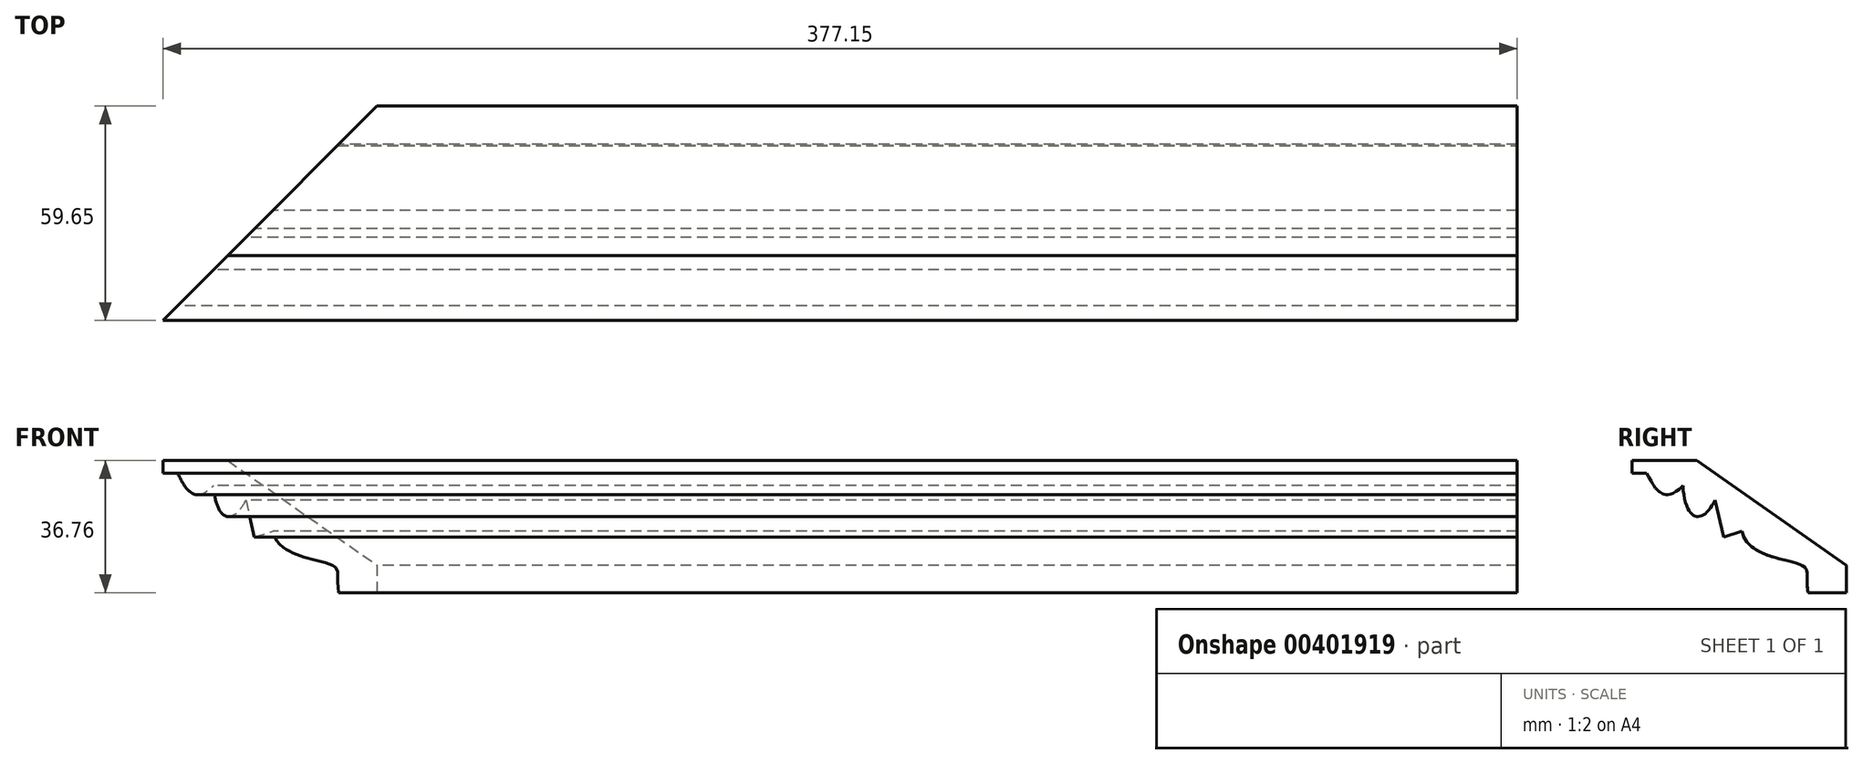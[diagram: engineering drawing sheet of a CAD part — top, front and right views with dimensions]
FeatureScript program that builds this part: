
annotation { "Feature Type Name" : "Feature", "Feature Type Description" : "" }
export const myFeature = defineFeature(function(context is Context, id is Id, definition is map)
    precondition{}
    {
        {
            var Q0;
            Q0=qCreatedBy(makeId("Right.planeOp"),FACE);
            var sketch = newSketch(context, id + "F0", { "sketchPlane" : qUnion([Q0])});
            skLineSegment(sketch, "E0", {"start": v(0, 7.62) * mm, "end": v(-41.61, 36.76) * mm});
            skLineSegment(sketch, "E1", {"start": v(-41.61, 36.76) * mm, "end": v(-59.65, 36.76) * mm});
            skLineSegment(sketch, "E2", {"start": v(-59.65, 36.76) * mm, "end": v(-59.65, 33.27) * mm});
            skLineSegment(sketch, "E3", {"start": v(-59.65, 33.27) * mm, "end": v(-55.58, 33.27) * mm});
            skLineSegment(sketch, "E4", {"start": v(0, 7.62) * mm, "end": v(0, 0) * mm});
            skLineSegment(sketch, "E5", {"start": v(0, 0) * mm, "end": v(-10.67, 0) * mm});
            skFitSpline(sketch, "E6", {"points": [v(-10.67, 0) * mm, v(-11.01, 5.96) * mm, v(-13.27, 7.99) * mm, v(-29.01, 17.09) * mm], "startDerivative": vector(-5.08, 29.03) * mm, "endDerivative": vector(-6.54, 39.72) * mm});
            skLineSegment(sketch, "E7", {"start": v(-29.01, 17.09) * mm, "end": v(-34.16, 15.48) * mm});
            skLineSegment(sketch, "E8", {"start": v(-34.16, 15.48) * mm, "end": v(-36.54, 25.8) * mm});
            skFitSpline(sketch, "E9", {"points": [v(-45.51, 29.77) * mm, v(-52.42, 28.4) * mm, v(-55.58, 33.27) * mm], "startDerivative": vector(-24.15, -24.15) * mm, "endDerivative": vector(-16.65, 31.11) * mm});
            skFitSpline(sketch, "E10", {"points": [v(-45.51, 29.77) * mm, v(-36.54, 25.8) * mm], "startDerivative": vector(2.07, -32.09) * mm, "endDerivative": vector(9.32, 20.18) * mm});
            skSolve(sketch);
        }
        {
            var Q0;
            Q0=qSketchRegion(id+"F0",true);
            extrude(context, id + "F1", {"entities" : qUnion([Q0]), "depth" : 228.6 * mm, "hasSecondDirection" : true, "secondDirectionOppositeDirection" : true, "secondDirectionDepth" : 177.8 * mm});
        }
        {
            var Q0;
            Q0=qCreatedBy(makeId("Top.planeOp"),FACE);
            var sketch = newSketch(context, id + "F2", { "sketchPlane" : qUnion([Q0])});
            skLineSegment(sketch, "E11", {"start": v(-88.9, 0) * mm, "end": v(88.9, 0) * mm, "construction": true});
            skLineSegment(sketch, "E12", {"start": v(0, 0) * mm, "end": v(0, -141.75) * mm, "construction": true});
            skLineSegment(sketch, "E13.MirrorCS", {"start": v(-88.9, 0) * mm, "end": v(-192.6, 0) * mm});
            skLineSegment(sketch, "E14.MirrorCS", {"start": v(-192.6, -103.7) * mm, "end": v(-88.9, 0) * mm});
            skLineSegment(sketch, "E15.MirrorCS", {"start": v(-192.6, 0) * mm, "end": v(-192.6, -103.7) * mm});
            skSolve(sketch);
        }
        {
            var Q0;
            Q0=qSketchRegion(id+"F2",true);
            extrude(context, id + "F3", {"entities" : qUnion([Q0]), "operationType" : NewBodyOperationType.REMOVE, "endBound" : BoundingType.THROUGH_ALL, "depth" : 25.4 * mm});
        }
    });
